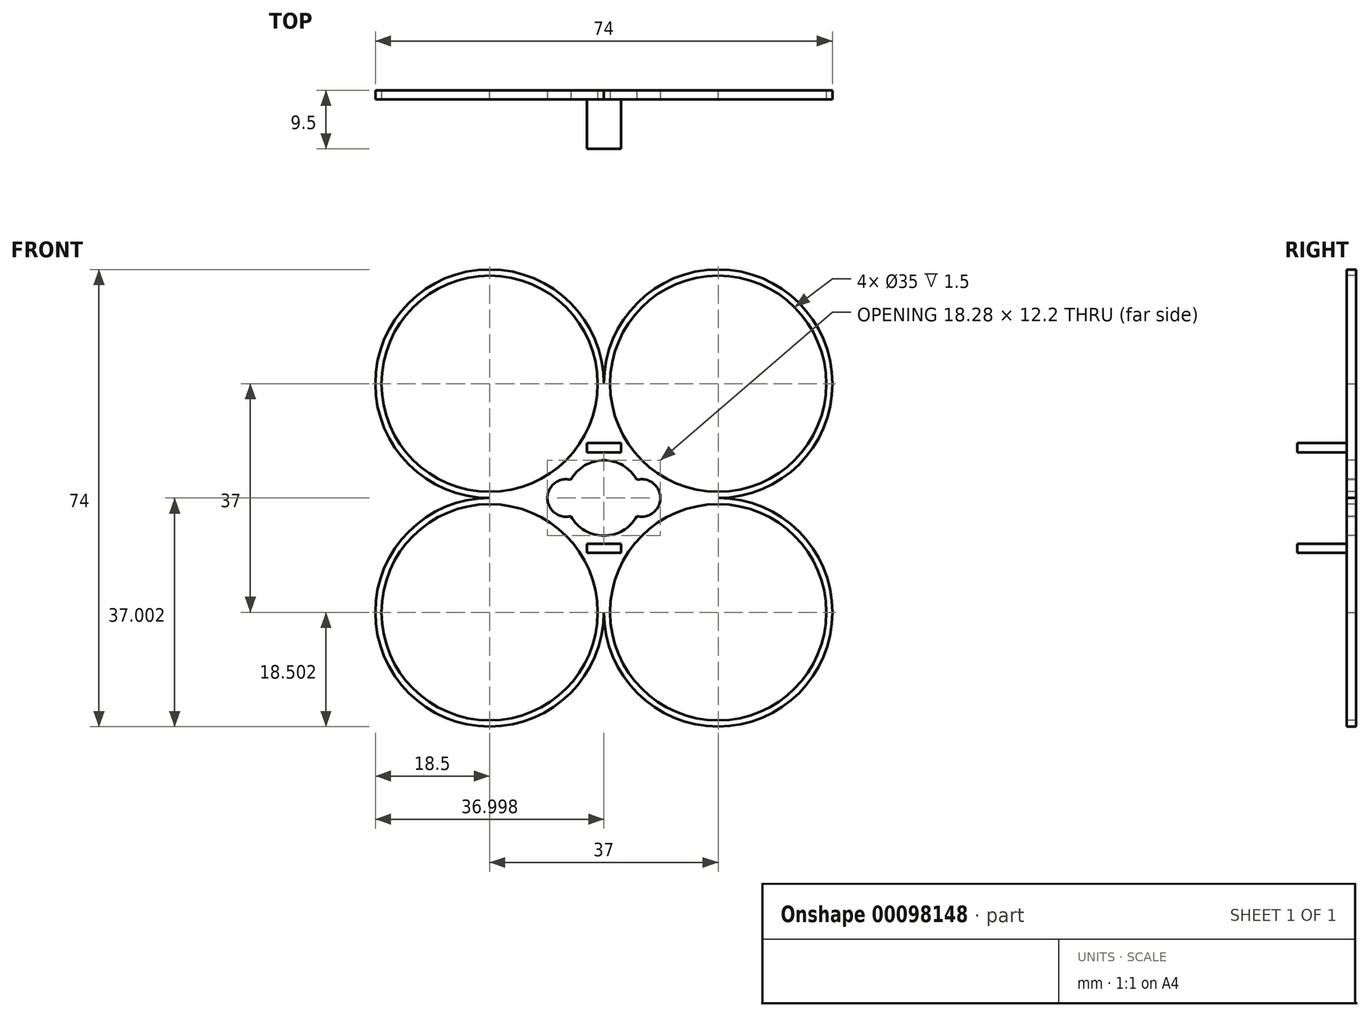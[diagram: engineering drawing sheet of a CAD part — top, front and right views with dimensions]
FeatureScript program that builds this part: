
annotation { "Feature Type Name" : "Feature", "Feature Type Description" : "" }
export const myFeature = defineFeature(function(context is Context, id is Id, definition is map)
    precondition{}
    {
        {
            var Q0;
            Q0=qCreatedBy(makeId("Front.planeOp"),FACE);
            var sketch = newSketch(context, id + "F0", { "sketchPlane" : qUnion([Q0])});
            skCircle(sketch, "E0", {"center": v(-25.9, 23.98) * mm, "radius": 18.5 * mm});
            skCircle(sketch, "E1.0.1.0", {"center": v(-25.9, 60.98) * mm, "radius": 18.5 * mm});
            skCircle(sketch, "E1.1.0.0", {"center": v(11.1, 23.98) * mm, "radius": 18.5 * mm});
            skCircle(sketch, "E1.1.1.0", {"center": v(11.1, 60.98) * mm, "radius": 18.5 * mm});
            skLineSegment(sketch, "E1.direction1", {"start": v(-25.9, 23.98) * mm, "end": v(11.1, 23.98) * mm, "construction": true});
            skLineSegment(sketch, "E1.direction2", {"start": v(-25.9, 23.98) * mm, "end": v(-25.9, 60.98) * mm, "construction": true});
            skSolve(sketch);
        }
        {
            var Q0;
            Q0 = qSketchRegion(id + "F0", true);
            extrude(context, id + "F1", {"entities" : qUnion([Q0]), "depth" : 1.5 * mm});
        }
        {
            var Q0;
            Q0=makeQuery(id+"F1.opExtrude","CAP_FACE",FACE,{"disambiguationData":[OSD([sQuery(id+"F0.wireOp",EDGE,"E0"),sQuery(id+"F0.wireOp",EDGE,"E1.0.1.0"),sQuery(id+"F0.wireOp",EDGE,"E1.1.0.0"),sQuery(id+"F0.wireOp",EDGE,"E1.1.1.0")])],"isStart":false});
            var sketch = newSketch(context, id + "F2", { "sketchPlane" : qUnion([Q0])});
            skCircle(sketch, "E2", {"center": v(-25.9, 60.98) * mm, "radius": 17.5 * mm});
            skCircle(sketch, "E3.0.1.0", {"center": v(-25.9, 23.98) * mm, "radius": 17.5 * mm});
            skCircle(sketch, "E3.1.0.0", {"center": v(11.1, 60.98) * mm, "radius": 17.5 * mm});
            skCircle(sketch, "E3.1.1.0", {"center": v(11.1, 23.98) * mm, "radius": 17.5 * mm});
            skLineSegment(sketch, "E3.direction1", {"start": v(-25.9, 60.98) * mm, "end": v(11.1, 60.98) * mm, "construction": true});
            skLineSegment(sketch, "E3.direction2", {"start": v(-25.9, 60.98) * mm, "end": v(-25.9, 23.98) * mm, "construction": true});
            skSolve(sketch);
        }
        {
            var Q0;
            Q0 = qSketchRegion(id + "F2", true);
            extrude(context, id + "F3", {"entities" : qUnion([Q0]), "operationType" : NewBodyOperationType.REMOVE, "endBound" : BoundingType.THROUGH_ALL, "oppositeDirection" : true, "depth" : 25 * mm});
        }
        {
            var Q0;
            Q0=makeQuery(id+"F1.opExtrude","CAP_FACE",FACE,{"disambiguationData":[OSD([sQuery(id+"F0.wireOp",EDGE,"E0"),sQuery(id+"F0.wireOp",EDGE,"E1.0.1.0"),sQuery(id+"F0.wireOp",EDGE,"E1.1.0.0"),sQuery(id+"F0.wireOp",EDGE,"E1.1.1.0")])],"isStart":false});
            var sketch = newSketch(context, id + "F4", { "sketchPlane" : qUnion([Q0])});
            skLineSegment(sketch, "E4.bottom", {"start": v(-10.14, 51.38) * mm, "end": v(-4.64, 51.38) * mm});
            skLineSegment(sketch, "E4.top", {"start": v(-10.14, 49.88) * mm, "end": v(-4.64, 49.88) * mm});
            skLineSegment(sketch, "E4.left", {"start": v(-10.14, 51.38) * mm, "end": v(-10.14, 49.88) * mm});
            skLineSegment(sketch, "E4.right", {"start": v(-4.64, 51.38) * mm, "end": v(-4.64, 49.88) * mm});
            skLineSegment(sketch, "E5.bottom", {"start": v(-10.14, 35.08) * mm, "end": v(-4.64, 35.08) * mm});
            skLineSegment(sketch, "E5.top", {"start": v(-10.14, 33.58) * mm, "end": v(-4.64, 33.58) * mm});
            skLineSegment(sketch, "E5.left", {"start": v(-10.14, 35.08) * mm, "end": v(-10.14, 33.58) * mm});
            skLineSegment(sketch, "E5.right", {"start": v(-4.64, 35.08) * mm, "end": v(-4.64, 33.58) * mm});
            skLineSegment(sketch, "E6", {"start": v(-25.9, 42.48) * mm, "end": v(11.1, 42.48) * mm});
            skLineSegment(sketch, "E7", {"start": v(-7.4, 23.98) * mm, "end": v(-7.4, 60.98) * mm});
            skSolve(sketch);
        }
        {
            var Q0;
            Q0 = qSketchRegion(id + "F4", true);
            extrude(context, id + "F5", {"entities" : qUnion([Q0]), "operationType" : NewBodyOperationType.ADD, "depth" : 8 * mm});
        }
        {
            var Q0;
            Q0=makeQuery(id+"F1.opExtrude","CAP_FACE",FACE,{"disambiguationData":[OSD([sQuery(id+"F0.wireOp",EDGE,"E0"),sQuery(id+"F0.wireOp",EDGE,"E1.0.1.0"),sQuery(id+"F0.wireOp",EDGE,"E1.1.0.0"),sQuery(id+"F0.wireOp",EDGE,"E1.1.1.0")])],"isStart":false});
            var sketch = newSketch(context, id + "F6", { "sketchPlane" : qUnion([Q0])});
            skArc(sketch, "E8", {"start": v(-12.73, 39.54) * mm, "mid": v(-7.39, 36.38) * mm, "end": v(-2.04, 39.54) * mm});
            skArc(sketch, "E9", {"start": v(-12.73, 45.43) * mm, "mid": v(-16.53, 42.48) * mm, "end": v(-12.73, 39.54) * mm});
            skArc(sketch, "E10", {"start": v(-2.04, 39.54) * mm, "mid": v(1.75, 42.48) * mm, "end": v(-2.04, 45.42) * mm});
            skArc(sketch, "E11.trimOffspring", {"start": v(-2.04, 45.42) * mm, "mid": v(-7.39, 48.58) * mm, "end": v(-12.73, 45.43) * mm});
            skSolve(sketch);
        }
        {
            var Q0;
            Q0 = qSketchRegion(id + "F6", true);
            extrude(context, id + "F7", {"entities" : qUnion([Q0]), "operationType" : NewBodyOperationType.REMOVE, "endBound" : BoundingType.THROUGH_ALL, "oppositeDirection" : true, "depth" : 25 * mm});
        }
    });
